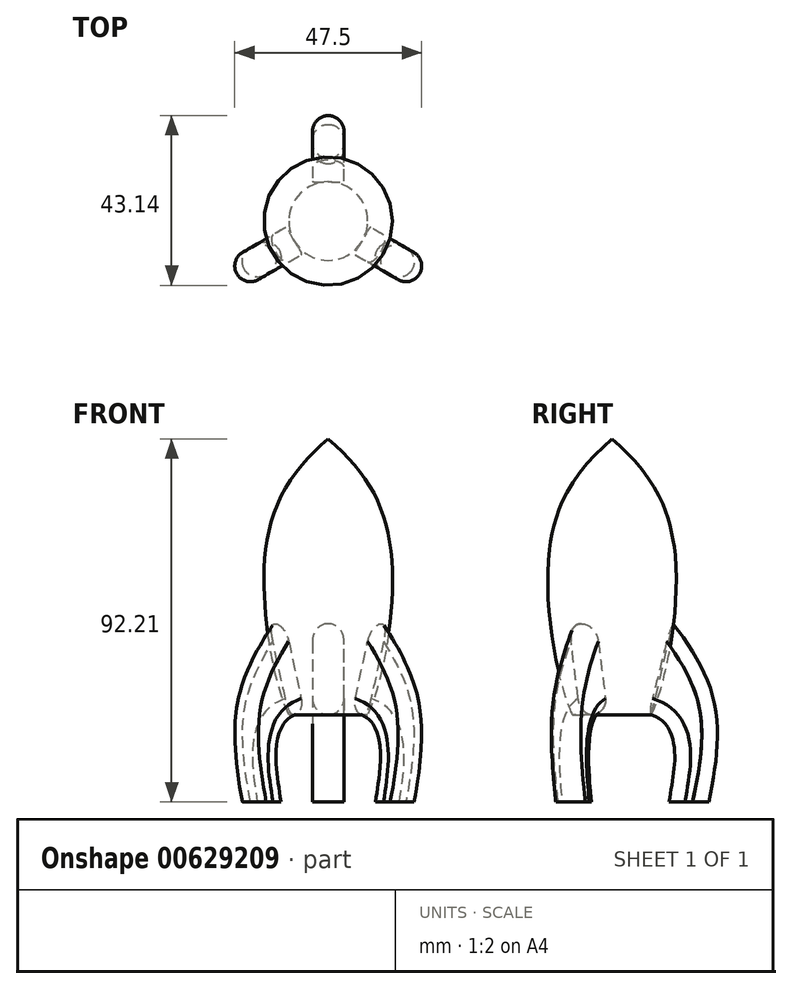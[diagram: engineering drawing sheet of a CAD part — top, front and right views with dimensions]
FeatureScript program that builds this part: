
annotation { "Feature Type Name" : "Feature", "Feature Type Description" : "" }
export const myFeature = defineFeature(function(context is Context, id is Id, definition is map)
    precondition{}
    {
        {
            var Q0;
            Q0=qCreatedBy(makeId("Front.planeOp"),FACE);
            var sketch = newSketch(context, id + "F0", { "sketchPlane" : qUnion([Q0])});
            skFitSpline(sketch, "E0", {"points": [v(0, 42.21) * mm, v(16, 13.21) * mm, v(10, -27.9) * mm], "startDerivative": vector(61.82, -52.97) * mm, "endDerivative": vector(-23.48, -52.71) * mm});
            skLineSegment(sketch, "E1", {"start": v(0, 42.21) * mm, "end": v(0, -27.79) * mm});
            skLineSegment(sketch, "E2", {"start": v(0, -27.79) * mm, "end": v(10, -27.9) * mm});
            skSolve(sketch);
        }
        {
            var Q0;
            Q0 = qSketchRegion(id + "F0", true);
            var Q1;
            Q1=sQuery(id+"F0.wireOp",EDGE,"E1");
            revolve(context, id + "F1", {"entities" : qUnion([Q0]), "axis" : qUnion([Q1]), "revolveType" : RevolveType.FULL});
        }
        {
            var Q0;
            Q0=qCreatedBy(makeId("Top.planeOp"),FACE);
            var sketch = newSketch(context, id + "F2", { "sketchPlane" : qUnion([Q0])});
            skLineSegment(sketch, "E3", {"start": v(-4, 30) * mm, "end": v(4, 30) * mm});
            skLineSegment(sketch, "E4", {"start": v(4, 30) * mm, "end": v(4, 2.3) * mm});
            skLineSegment(sketch, "E5", {"start": v(4, 2.3) * mm, "end": v(27.98, -11.54) * mm});
            skLineSegment(sketch, "E6", {"start": v(27.98, -11.54) * mm, "end": v(23.98, -18.46) * mm});
            skLineSegment(sketch, "E7", {"start": v(23.98, -18.46) * mm, "end": v(0, -4.62) * mm});
            skLineSegment(sketch, "E8", {"start": v(0, -4.62) * mm, "end": v(-23.98, -18.46) * mm});
            skLineSegment(sketch, "E9", {"start": v(-23.98, -18.46) * mm, "end": v(-27.98, -11.54) * mm});
            skLineSegment(sketch, "E10", {"start": v(-27.98, -11.54) * mm, "end": v(-4, 2.3) * mm});
            skLineSegment(sketch, "E11", {"start": v(-4, 2.3) * mm, "end": v(-4, 30) * mm});
            skCircle(sketch, "E12", {"center": v(0, 0) * mm, "radius": 4.62 * mm, "construction": true});
            skSolve(sketch);
        }
        {
            var Q0;
            Q0=makeQuery(id+"F2.imprint","IMPRINT",FACE,{"disambiguationData":[TD([[makeQuery(id+"F2.imprint","IMPRINT",EDGE,{"derivedFrom":sQuery(id+"F2.wireOp",EDGE,"E3")}),-1.0]])]});
            var Q1;
            Q1=sQuery(id+"F2.wireOp",EDGE,"E12");
            var Q2;
            Q2=sQuery(id+"F2.wireOp",EDGE,"E4");
            extrude(context, id + "F3", {"entities" : qUnion([Q0]), "surfaceEntities" : qUnion([Q1, Q2]), "oppositeDirection" : true, "depth" : 50 * mm, "offsetDistance" : 25 * mm});
        }
        {
            var Q0;
            Q0=qCreatedBy(makeId("Right.planeOp"),FACE);
            var sketch = newSketch(context, id + "F4", { "sketchPlane" : qUnion([Q0])});
            skFitSpline(sketch, "E13", {"points": [v(15.52, -4.75) * mm, v(26.05, -25) * mm, v(24.59, -50) * mm], "startDerivative": vector(29.84, -39.18) * mm, "endDerivative": vector(-10.9, -51.5) * mm});
            skFitSpline(sketch, "E14", {"points": [v(10, -27.9) * mm, v(15.79, -35.99) * mm, v(14.47, -50) * mm], "startDerivative": vector(27.89, -9.3) * mm, "endDerivative": vector(-6.56, -36.82) * mm});
            skLineSegment(sketch, "E15", {"start": v(10, -27.9) * mm, "end": v(15.52, -4.75) * mm});
            skLineSegment(sketch, "E16", {"start": v(14.47, -50) * mm, "end": v(24.59, -50) * mm});
            skLineSegment(sketch, "E17", {"start": v(0, 0) * mm, "end": v(0, -51.1) * mm, "construction": true});
            skSolve(sketch);
        }
        {
            var Q0;
            Q0 = qSketchRegion(id + "F4", true);
            var Q1;
            Q1=sQuery(id+"F4.wireOp",EDGE,"E17");
            revolve(context, id + "F5", {"entities" : qUnion([Q0]), "axis" : qUnion([Q1]), "revolveType" : RevolveType.FULL});
        }
        {
            var Q0;
            Q0=makeQuery(id+"F3.opExtrude","SWEPT_BODY",BODY,{"disambiguationData":[OSD([sQuery(id+"F2.wireOp",EDGE,"E3"),sQuery(id+"F2.wireOp",EDGE,"E4"),sQuery(id+"F2.wireOp",EDGE,"E5"),sQuery(id+"F2.wireOp",EDGE,"E6"),sQuery(id+"F2.wireOp",EDGE,"E7"),sQuery(id+"F2.wireOp",EDGE,"E8"),sQuery(id+"F2.wireOp",EDGE,"E9"),sQuery(id+"F2.wireOp",EDGE,"E10"),sQuery(id+"F2.wireOp",EDGE,"E11")])]});
            var Q1;
            Q1=makeQuery(id+"F5.opRevolve","SWEPT_BODY",BODY,{"disambiguationData":[OSD([sQuery(id+"F4.wireOp",EDGE,"E13"),sQuery(id+"F4.wireOp",EDGE,"E14"),sQuery(id+"F4.wireOp",EDGE,"E15"),sQuery(id+"F4.wireOp",EDGE,"E16")])]});
            booleanBodies(context, id + "F6", {"operationType" : BooleanOperationType.INTERSECTION, "tools" : qUnion([Q0, Q1])});
        }
        {
            var Q0;
            Q0=makeQuery(id+"F6.opBoolean","INTERSECT",EDGE,{"derivedFrom":[makeQuery(id+"F3.opExtrude","SWEPT_FACE",FACE,{"disambiguationData":[OSD([sQuery(id+"F2.wireOp",EDGE,"E4")])]}),makeQuery(id+"F5.opRevolve","SWEPT_FACE",FACE,{"disambiguationData":[OSD([sQuery(id+"F4.wireOp",EDGE,"E13")])]})]});
            var Q1;
            Q1=makeQuery(id+"F6.opBoolean","INTERSECT",EDGE,{"derivedFrom":[makeQuery(id+"F3.opExtrude","SWEPT_FACE",FACE,{"disambiguationData":[OSD([sQuery(id+"F2.wireOp",EDGE,"E5")])]}),makeQuery(id+"F5.opRevolve","SWEPT_FACE",FACE,{"disambiguationData":[OSD([sQuery(id+"F4.wireOp",EDGE,"E13")])]})]});
            var Q2;
            Q2=makeQuery(id+"F6.opBoolean","INTERSECT",EDGE,{"derivedFrom":[makeQuery(id+"F3.opExtrude","SWEPT_FACE",FACE,{"disambiguationData":[OSD([sQuery(id+"F2.wireOp",EDGE,"E7")])]}),makeQuery(id+"F5.opRevolve","SWEPT_FACE",FACE,{"disambiguationData":[OSD([sQuery(id+"F4.wireOp",EDGE,"E13")])]})]});
            var Q3;
            Q3=makeQuery(id+"F6.opBoolean","INTERSECT",EDGE,{"derivedFrom":[makeQuery(id+"F3.opExtrude","SWEPT_FACE",FACE,{"disambiguationData":[OSD([sQuery(id+"F2.wireOp",EDGE,"E11")])]}),makeQuery(id+"F5.opRevolve","SWEPT_FACE",FACE,{"disambiguationData":[OSD([sQuery(id+"F4.wireOp",EDGE,"E13")])]})]});
            var Q4;
            Q4=makeQuery(id+"F6.opBoolean","INTERSECT",EDGE,{"derivedFrom":[makeQuery(id+"F3.opExtrude","SWEPT_FACE",FACE,{"disambiguationData":[OSD([sQuery(id+"F2.wireOp",EDGE,"E10")])]}),makeQuery(id+"F5.opRevolve","SWEPT_FACE",FACE,{"disambiguationData":[OSD([sQuery(id+"F4.wireOp",EDGE,"E13")])]})]});
            var Q5;
            Q5=makeQuery(id+"F6.opBoolean","INTERSECT",EDGE,{"derivedFrom":[makeQuery(id+"F3.opExtrude","SWEPT_FACE",FACE,{"disambiguationData":[OSD([sQuery(id+"F2.wireOp",EDGE,"E8")])]}),makeQuery(id+"F5.opRevolve","SWEPT_FACE",FACE,{"disambiguationData":[OSD([sQuery(id+"F4.wireOp",EDGE,"E13")])]})]});
            var Q6;
            Q6=makeQuery(id+"F6.opBoolean","INTERSECT",EDGE,{"derivedFrom":[makeQuery(id+"F3.opExtrude","SWEPT_FACE",FACE,{"disambiguationData":[OSD([sQuery(id+"F2.wireOp",EDGE,"E10")])]}),makeQuery(id+"F5.opRevolve","SWEPT_FACE",FACE,{"disambiguationData":[OSD([sQuery(id+"F4.wireOp",EDGE,"E14")])]})]});
            var Q7;
            Q7=makeQuery(id+"F6.opBoolean","INTERSECT",EDGE,{"derivedFrom":[makeQuery(id+"F3.opExtrude","SWEPT_FACE",FACE,{"disambiguationData":[OSD([sQuery(id+"F2.wireOp",EDGE,"E8")])]}),makeQuery(id+"F5.opRevolve","SWEPT_FACE",FACE,{"disambiguationData":[OSD([sQuery(id+"F4.wireOp",EDGE,"E14")])]})]});
            var Q8;
            Q8=makeQuery(id+"F6.opBoolean","INTERSECT",EDGE,{"derivedFrom":[makeQuery(id+"F3.opExtrude","SWEPT_FACE",FACE,{"disambiguationData":[OSD([sQuery(id+"F2.wireOp",EDGE,"E11")])]}),makeQuery(id+"F5.opRevolve","SWEPT_FACE",FACE,{"disambiguationData":[OSD([sQuery(id+"F4.wireOp",EDGE,"E14")])]})]});
            var Q9;
            Q9=makeQuery(id+"F6.opBoolean","INTERSECT",EDGE,{"derivedFrom":[makeQuery(id+"F3.opExtrude","SWEPT_FACE",FACE,{"disambiguationData":[OSD([sQuery(id+"F2.wireOp",EDGE,"E4")])]}),makeQuery(id+"F5.opRevolve","SWEPT_FACE",FACE,{"disambiguationData":[OSD([sQuery(id+"F4.wireOp",EDGE,"E14")])]})]});
            var Q10;
            Q10=makeQuery(id+"F6.opBoolean","INTERSECT",EDGE,{"derivedFrom":[makeQuery(id+"F3.opExtrude","SWEPT_FACE",FACE,{"disambiguationData":[OSD([sQuery(id+"F2.wireOp",EDGE,"E7")])]}),makeQuery(id+"F5.opRevolve","SWEPT_FACE",FACE,{"disambiguationData":[OSD([sQuery(id+"F4.wireOp",EDGE,"E14")])]})]});
            var Q11;
            Q11=makeQuery(id+"F6.opBoolean","INTERSECT",EDGE,{"derivedFrom":[makeQuery(id+"F3.opExtrude","SWEPT_FACE",FACE,{"disambiguationData":[OSD([sQuery(id+"F2.wireOp",EDGE,"E5")])]}),makeQuery(id+"F5.opRevolve","SWEPT_FACE",FACE,{"disambiguationData":[OSD([sQuery(id+"F4.wireOp",EDGE,"E14")])]})]});
            fillet(context, id + "F7", {"entities" : qUnion([Q0, Q1, Q2, Q3, Q4, Q5, Q6, Q7, Q8, Q9, Q10, Q11]), "radius" : 4 * mm, "tangentPropagation" : true, "allowEdgeOverflow" : false});
        }
    });
